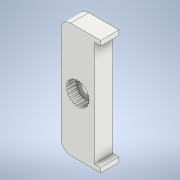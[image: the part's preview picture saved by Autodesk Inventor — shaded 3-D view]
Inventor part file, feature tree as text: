
AUTODESK INVENTOR PART (.ipt)
format: ipt  version: 2022 (Build 260153000, 153)  size: 188,416 bytes
history: mixed  units: in
note: dims shown in document units (in); Inventor stores cm internally (conversion verified against a paired STEP export)
features: sketch x3, extrude x2, fillet x2, imported_body x1
ambient origin geometry x8: Origin, YZ Plane, XZ Plane, XY Plane, X Axis, Y Axis, Z Axis, Center Point
bodies: Solid1 (imported_parasolid), Body1 (imported_parasolid)
feature tree (8):
  sketch  "스케치1"
  extrude  "돌출1"  Depth=0.6902in
  extrude  "돌출2"  Depth=0.1969in TaperAngle=0.0deg
  fillet  "모깎기1"  Radius=0.2756in
  fillet  "모깎기2"  Radius=0.4724in
  sketch  "스케치2"
  sketch  "스케치3"
  imported_body  NMx_Import_Brep_tag  [imported B-rep: ~60 faces, bbox_mm=[8.3, 24.0, 3.8]]
